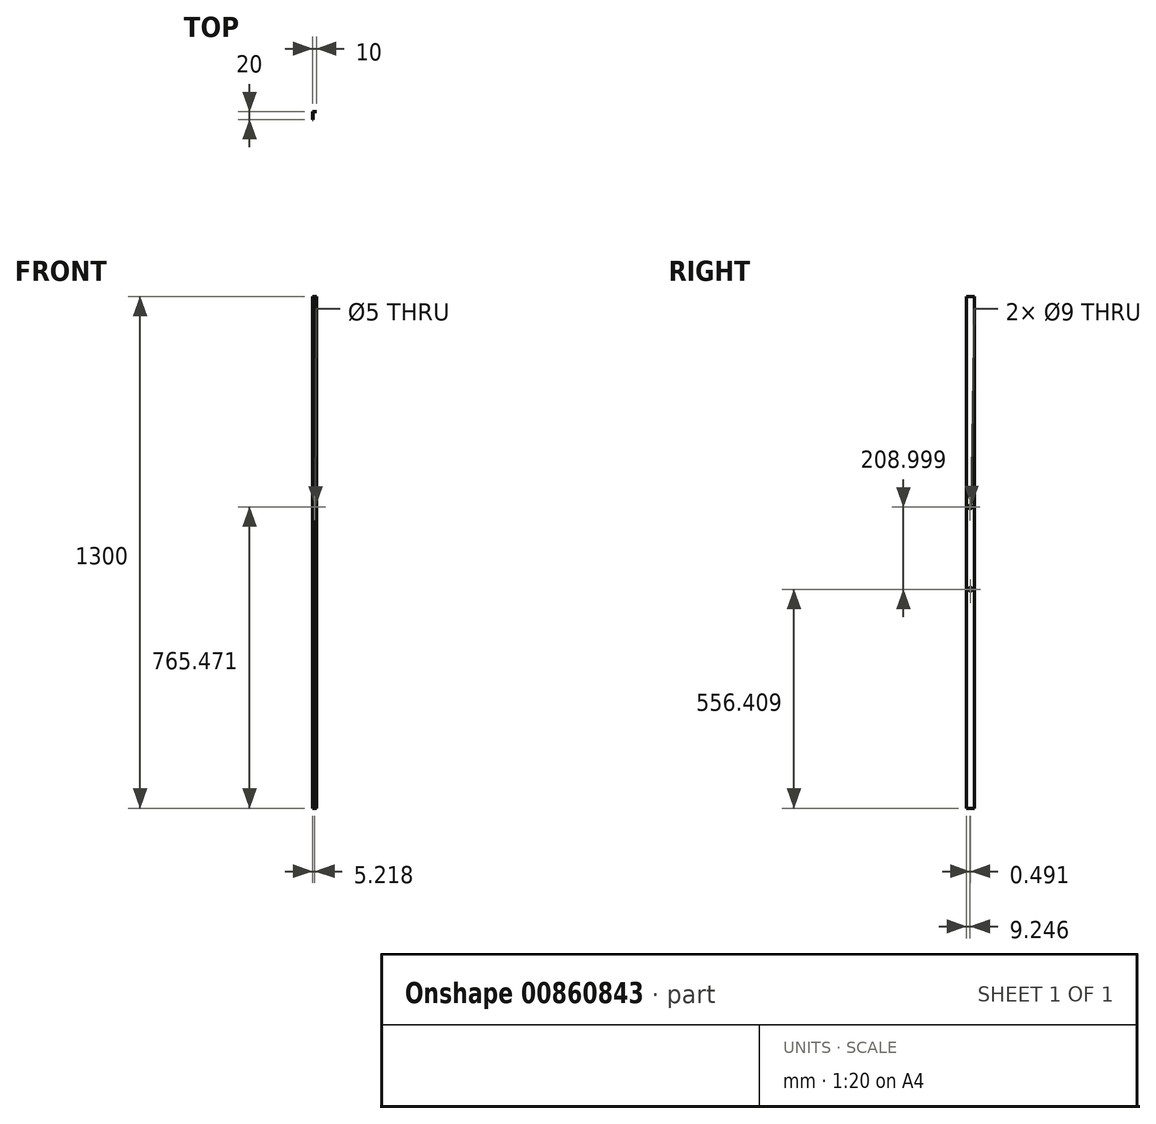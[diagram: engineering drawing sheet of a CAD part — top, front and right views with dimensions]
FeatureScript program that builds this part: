
annotation { "Feature Type Name" : "Feature", "Feature Type Description" : "" }
export const myFeature = defineFeature(function(context is Context, id is Id, definition is map)
    precondition{}
    {
        {
            var Q0;
            Q0=qCreatedBy(makeId("Top.planeOp"),FACE);
            var sketch = newSketch(context, id + "F0", { "sketchPlane" : qUnion([Q0])});
            skLineSegment(sketch, "E0.bottom", {"start": v(-57.22, -40.3) * mm, "end": v(-56.72, -40.3) * mm});
            skLineSegment(sketch, "E0.top", {"start": v(-57.22, -20.3) * mm, "end": v(-56.72, -20.3) * mm});
            skLineSegment(sketch, "E0.left", {"start": v(-57.22, -40.3) * mm, "end": v(-57.22, -20.3) * mm});
            skLineSegment(sketch, "E0.right", {"start": v(-56.72, -40.3) * mm, "end": v(-56.72, -20.3) * mm});
            skLineSegment(sketch, "E1.bottom", {"start": v(-57.22, -20.3) * mm, "end": v(-47.22, -20.3) * mm});
            skLineSegment(sketch, "E1.top", {"start": v(-57.22, -20.8) * mm, "end": v(-47.22, -20.8) * mm});
            skLineSegment(sketch, "E1.left", {"start": v(-57.22, -20.3) * mm, "end": v(-57.22, -20.8) * mm});
            skLineSegment(sketch, "E1.right", {"start": v(-47.22, -20.3) * mm, "end": v(-47.22, -20.8) * mm});
            skSolve(sketch);
        }
        {
            var Q0;
            {var subQ0=sQuery(id+"F0.wireOp",EDGE,"E0.bottom");Q0=makeQuery(id+"F0.imprint","IMPRINT",FACE,{"disambiguationData":[TD([[makeQuery(id+"F0.imprint","IMPRINT",EDGE,{"derivedFrom":subQ0}),1.0]])]});}
            var Q1;
            {var subQ5=sQuery(id+"F0.wireOp",EDGE,"E1.left");Q1=makeQuery(id+"F0.imprint","IMPRINT",FACE,{"disambiguationData":[TD([[makeQuery(id+"F0.imprint","IMPRINT",EDGE,{"derivedFrom":subQ5}),1.0]])]});}
            var Q2;
            {var subQ5=sQuery(id+"F0.wireOp",EDGE,"E1.right");Q2=makeQuery(id+"F0.imprint","IMPRINT",FACE,{"disambiguationData":[TD([[makeQuery(id+"F0.imprint","IMPRINT",EDGE,{"derivedFrom":subQ5}),-1.0]])]});}
            extrude(context, id + "F1", {"entities" : qUnion([Q0, Q1, Q2]), "depth" : 1300 * mm, "offsetDistance" : 25 * mm});
        }
        {
            var Q0;
            Q0=makeQuery(id+"F1.opExtrude","SWEPT_FACE",FACE,{"disambiguationData":[OSD([sQuery(id+"F0.wireOp",EDGE,"E0.left"),sQuery(id+"F0.wireOp",EDGE,"E1.left")])]});
            var sketch = newSketch(context, id + "F2", { "sketchPlane" : qUnion([Q0])});
            skCircle(sketch, "E2", {"center": v(31.05, 765.4) * mm, "radius": 4.5 * mm});
            skSolve(sketch);
        }
        {
            var Q0;
            Q0 = qSketchRegion(id + "F2", true);
            extrude(context, id + "F3", {"entities" : qUnion([Q0]), "operationType" : NewBodyOperationType.REMOVE, "oppositeDirection" : true, "depth" : 25 * mm, "offsetDistance" : 25 * mm});
        }
        {
            var Q0;
            Q0=makeQuery(id+"F1.opExtrude","SWEPT_FACE",FACE,{"disambiguationData":[OSD([sQuery(id+"F0.wireOp",EDGE,"E1.bottom")])]});
            var sketch = newSketch(context, id + "F4", { "sketchPlane" : qUnion([Q0])});
            skCircle(sketch, "E3", {"center": v(52, 765.47) * mm, "radius": 2.5 * mm});
            skSolve(sketch);
        }
        {
            var Q0;
            Q0 = qSketchRegion(id + "F4", true);
            extrude(context, id + "F5", {"entities" : qUnion([Q0]), "operationType" : NewBodyOperationType.REMOVE, "oppositeDirection" : true, "depth" : 25 * mm, "offsetDistance" : 25 * mm});
        }
        {
            var Q0;
            Q0=makeQuery(id+"F1.opExtrude","SWEPT_FACE",FACE,{"disambiguationData":[OSD([sQuery(id+"F0.wireOp",EDGE,"E0.left"),sQuery(id+"F0.wireOp",EDGE,"E1.left")])]});
            var sketch = newSketch(context, id + "F6", { "sketchPlane" : qUnion([Q0])});
            skCircle(sketch, "E4", {"center": v(30.56, 556.4) * mm, "radius": 4.5 * mm});
            skSolve(sketch);
        }
        {
            var Q0;
            Q0 = qSketchRegion(id + "F6", true);
            extrude(context, id + "F7", {"entities" : qUnion([Q0]), "operationType" : NewBodyOperationType.REMOVE, "oppositeDirection" : true, "depth" : 25 * mm, "offsetDistance" : 25 * mm});
        }
    });
